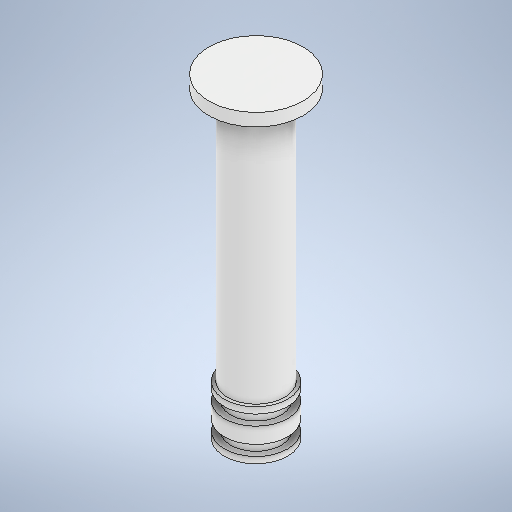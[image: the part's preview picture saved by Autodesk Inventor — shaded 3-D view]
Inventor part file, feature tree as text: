
AUTODESK INVENTOR PART (.ipt)
format: ipt  version: 2025.2 (Build 292293000, 293)  size: 278,528 bytes
history: native  units: mm
features: extrude x7, sketch x7
ambient origin geometry x8: Origin, YZ Plane, XZ Plane, XY Plane, X Axis, Y Axis, Z Axis, Center Point
bodies: Solid1 (feature_tree)
feature tree (14):
  extrude  "Extrusion1"  Depth=80.0mm TaperAngle=0.0deg
  extrude  "Extrusion2"  Depth=4.0mm TaperAngle=0.0deg
  extrude  "Extrusion3"  Depth=2.0mm TaperAngle=0.0deg
  extrude  "Extrusion4"  Depth=3.3mm TaperAngle=0.0deg
  extrude  "Extrusion5"  Depth=5.0mm TaperAngle=0.0deg
  extrude  "Extrusion6"  Depth=3.3mm TaperAngle=0.0deg
  extrude  "Extrusion7"  Depth=2.0mm TaperAngle=0.0deg
  sketch  "Sketch1"  dims[d0=18.0mm d1=80.0mm d2=0.0mm]
  sketch  "Sketch2"  dims[d3=29.7mm d4=4.0mm d5=0.0mm]
  sketch  "Sketch3"  dims[d6=20.0mm d7=2.0mm d8=0.0mm]
  sketch  "Sketch4"  dims[d9=16.0mm d10=3.3mm d11=0.0mm]
  sketch  "Sketch5"  dims[d12=20.0mm d13=5.0mm d14=0.0mm]
  sketch  "Sketch7"  dims[d15=16.0mm d16=3.3mm d17=0.0mm]
  sketch  "Sketch8"  dims[d18=20.0mm d19=2.0mm d20=0.0mm]
